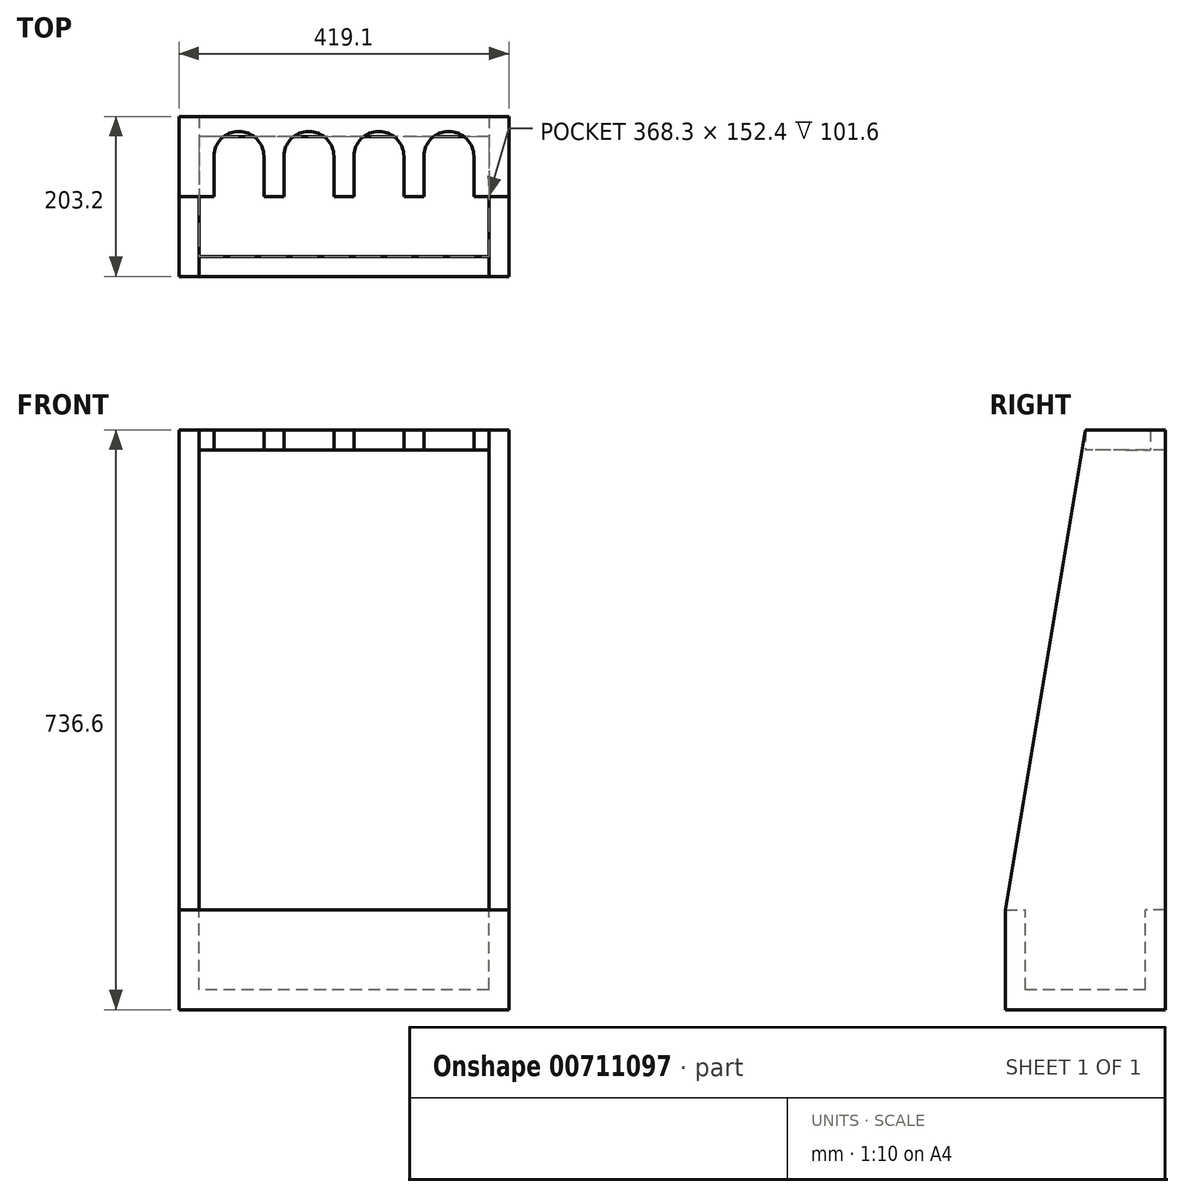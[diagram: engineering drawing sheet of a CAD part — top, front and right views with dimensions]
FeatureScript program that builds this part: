
annotation { "Feature Type Name" : "Feature", "Feature Type Description" : "" }
export const myFeature = defineFeature(function(context is Context, id is Id, definition is map)
    precondition{}
    {
        {
            var Q0;
            Q0=qCreatedBy(makeId("Top.planeOp"),FACE);
            var sketch = newSketch(context, id + "F0", { "sketchPlane" : qUnion([Q0])});
            skLineSegment(sketch, "E0.bottom", {"start": v(184.15, 50.8) * mm, "end": v(-184.15, 50.8) * mm});
            skLineSegment(sketch, "E0.top", {"start": v(184.15, -50.8) * mm, "end": v(-184.15, -50.8) * mm});
            skLineSegment(sketch, "E0.left", {"start": v(184.15, 50.8) * mm, "end": v(184.15, -50.8) * mm});
            skLineSegment(sketch, "E0.right", {"start": v(-184.15, 50.8) * mm, "end": v(-184.15, -50.8) * mm});
            skPoint(sketch, "E0.middle", {"position": v(0, 0) * mm});
            skCircle(sketch, "E1", {"center": v(-133.35, 0) * mm, "radius": 31.75 * mm});
            skLineSegment(sketch, "E2", {"start": v(-165.1, 0) * mm, "end": v(-165.1, -50.8) * mm});
            skLineSegment(sketch, "E3", {"start": v(-101.6, 0) * mm, "end": v(-101.6, -50.8) * mm});
            skCircle(sketch, "E4.1.0.0", {"center": v(-44.45, 0) * mm, "radius": 31.75 * mm});
            skCircle(sketch, "E4.2.0.0", {"center": v(44.45, 0) * mm, "radius": 31.75 * mm});
            skCircle(sketch, "E4.3.0.0", {"center": v(133.35, 0) * mm, "radius": 31.75 * mm});
            skLineSegment(sketch, "E4.direction1", {"start": v(-133.35, 0) * mm, "end": v(-44.45, 0) * mm, "construction": true});
            skLineSegment(sketch, "E5.1.0.0", {"start": v(-12.7, 0) * mm, "end": v(-12.7, -50.8) * mm});
            skLineSegment(sketch, "E5.1.0.1", {"start": v(-76.2, 0) * mm, "end": v(-76.2, -50.8) * mm});
            skLineSegment(sketch, "E5.2.0.0", {"start": v(76.2, 0) * mm, "end": v(76.2, -50.8) * mm});
            skLineSegment(sketch, "E5.2.0.1", {"start": v(12.7, 0) * mm, "end": v(12.7, -50.8) * mm});
            skLineSegment(sketch, "E5.3.0.0", {"start": v(165.1, 0) * mm, "end": v(165.1, -50.8) * mm});
            skLineSegment(sketch, "E5.3.0.1", {"start": v(101.6, 0) * mm, "end": v(101.6, -50.8) * mm});
            skLineSegment(sketch, "E5.direction1", {"start": v(-165.1, -50.8) * mm, "end": v(-76.2, -50.8) * mm, "construction": true});
            skSolve(sketch);
        }
        {
            var Q0;
            Q0=makeQuery(id+"F0.imprint","IMPRINT",FACE,{"disambiguationData":[TD([[makeQuery(id+"F0.imprint","IMPRINT",EDGE,{"derivedFrom":sQuery(id+"F0.wireOp",EDGE,"E0.bottom")}),1.0]])]});
            extrude(context, id + "F1", {"entities" : qUnion([Q0]), "depth" : 25.4 * mm, "offsetDistance" : 25.4 * mm});
        }
        {
            var Q0;
            Q0=makeQuery(id+"F1.opExtrude","SWEPT_FACE",FACE,{"disambiguationData":[OSD([sQuery(id+"F0.wireOp",EDGE,"E0.left")])]});
            var sketch = newSketch(context, id + "F2", { "sketchPlane" : qUnion([Q0])});
            skLineSegment(sketch, "E6", {"start": v(50.8, 25.4) * mm, "end": v(50.8, -685.8) * mm});
            skLineSegment(sketch, "E7", {"start": v(50.8, -685.8) * mm, "end": v(-152.4, -685.8) * mm});
            skLineSegment(sketch, "E8", {"start": v(-50.8, 25.4) * mm, "end": v(50.8, 25.4) * mm});
            skLineSegment(sketch, "E9", {"start": v(-152.4, -685.8) * mm, "end": v(-152.4, -584.2) * mm});
            skLineSegment(sketch, "E10", {"start": v(-152.4, -584.2) * mm, "end": v(-50.8, 25.4) * mm});
            skSolve(sketch);
        }
        {
            var Q0;
            Q0 = qSketchRegion(id + "F2", true);
            extrude(context, id + "F3", {"entities" : qUnion([Q0]), "operationType" : NewBodyOperationType.ADD, "depth" : 25.4 * mm, "offsetDistance" : 25.4 * mm});
        }
        {
            var Q0;
            Q0=makeQuery(id+"F1.opExtrude","SWEPT_BODY",BODY,{"disambiguationData":[OSD([sQuery(id+"F0.wireOp",EDGE,"E0.bottom"),sQuery(id+"F0.wireOp",EDGE,"E0.top"),sQuery(id+"F0.wireOp",EDGE,"E0.left"),sQuery(id+"F0.wireOp",EDGE,"E0.right"),sQuery(id+"F0.wireOp",EDGE,"E1"),sQuery(id+"F0.wireOp",EDGE,"E2"),sQuery(id+"F0.wireOp",EDGE,"E3"),sQuery(id+"F0.wireOp",EDGE,"E4.1.0.0"),sQuery(id+"F0.wireOp",EDGE,"E4.2.0.0"),sQuery(id+"F0.wireOp",EDGE,"E4.3.0.0"),sQuery(id+"F0.wireOp",EDGE,"E5.1.0.0"),sQuery(id+"F0.wireOp",EDGE,"E5.1.0.1"),sQuery(id+"F0.wireOp",EDGE,"E5.2.0.0"),sQuery(id+"F0.wireOp",EDGE,"E5.2.0.1"),sQuery(id+"F0.wireOp",EDGE,"E5.3.0.0"),sQuery(id+"F0.wireOp",EDGE,"E5.3.0.1")])]});
            var Q1;
            Q1=qCreatedBy(makeId("Right.planeOp"),FACE);
            mirror(context, id + "F4", {"operationType" : NewBodyOperationType.ADD, "entities" : qUnion([Q0]), "mirrorPlane" : qUnion([Q1])});
        }
        {
            var Q0;
            Q0=makeQuery(id+"F4.opPattern","COPY",FACE,{"derivedFrom":makeQuery(id+"F3.opExtrude","CAP_FACE",FACE,{"disambiguationData":[OSD([sQuery(id+"F2.wireOp",EDGE,"E6"),sQuery(id+"F2.wireOp",EDGE,"E7"),sQuery(id+"F2.wireOp",EDGE,"E8"),sQuery(id+"F2.wireOp",EDGE,"E9"),sQuery(id+"F2.wireOp",EDGE,"E10")])],"isStart":true}),"instanceName":"1"});
            var sketch = newSketch(context, id + "F5", { "sketchPlane" : qUnion([Q0])});
            skLineSegment(sketch, "E11.bottom", {"start": v(-152.4, -685.8) * mm, "end": v(-127, -685.8) * mm});
            skLineSegment(sketch, "E11.top", {"start": v(-152.4, -584.2) * mm, "end": v(-127, -584.2) * mm});
            skLineSegment(sketch, "E11.left", {"start": v(-152.4, -685.8) * mm, "end": v(-152.4, -584.2) * mm});
            skLineSegment(sketch, "E11.right", {"start": v(-127, -685.8) * mm, "end": v(-127, -584.2) * mm});
            skLineSegment(sketch, "E12.bottom", {"start": v(50.8, -685.8) * mm, "end": v(25.4, -685.8) * mm});
            skLineSegment(sketch, "E12.top", {"start": v(50.8, -584.2) * mm, "end": v(25.4, -584.2) * mm});
            skLineSegment(sketch, "E12.left", {"start": v(50.8, -685.8) * mm, "end": v(50.8, -584.2) * mm});
            skLineSegment(sketch, "E12.right", {"start": v(25.4, -685.8) * mm, "end": v(25.4, -584.2) * mm});
            skSolve(sketch);
        }
        {
            var Q0;
            Q0 = qSketchRegion(id + "F5", true);
            extrude(context, id + "F6", {"entities" : qUnion([Q0]), "operationType" : NewBodyOperationType.ADD, "endBound" : BoundingType.UP_TO_NEXT, "depth" : 25.4 * mm, "offsetDistance" : 25.4 * mm});
        }
        {
            var Q0;
            {var subQ0=makeQuery(id+"F3.opExtrude","SWEPT_FACE",FACE,{"disambiguationData":[OSD([sQuery(id+"F2.wireOp",EDGE,"E7")])]});Q0=makeQuery(id+"F6.boolean.opBoolean","MERGE",FACE,{"derivedFrom":[subQ0,makeQuery(id+"F4.opPattern","COPY",FACE,{"derivedFrom":subQ0,"instanceName":"1"}),makeQuery(id+"F6.opExtrude","SWEPT_FACE",FACE,{"disambiguationData":[OSD([sQuery(id+"F5.wireOp",EDGE,"E11.bottom")])]}),makeQuery(id+"F6.opExtrude","SWEPT_FACE",FACE,{"disambiguationData":[OSD([sQuery(id+"F5.wireOp",EDGE,"E12.bottom")])]})]});}
            var sketch = newSketch(context, id + "F7", { "sketchPlane" : qUnion([Q0])});
            skLineSegment(sketch, "E13.bottom", {"start": v(-209.55, 152.4) * mm, "end": v(209.55, 152.4) * mm});
            skLineSegment(sketch, "E13.top", {"start": v(-209.55, -50.8) * mm, "end": v(209.55, -50.8) * mm});
            skLineSegment(sketch, "E13.left", {"start": v(-209.55, 152.4) * mm, "end": v(-209.55, -50.8) * mm});
            skLineSegment(sketch, "E13.right", {"start": v(209.55, 152.4) * mm, "end": v(209.55, -50.8) * mm});
            skSolve(sketch);
        }
        {
            var Q0;
            Q0 = qSketchRegion(id + "F7", true);
            extrude(context, id + "F8", {"entities" : qUnion([Q0]), "operationType" : NewBodyOperationType.ADD, "depth" : 25.4 * mm, "offsetDistance" : 25.4 * mm});
        }
    });
